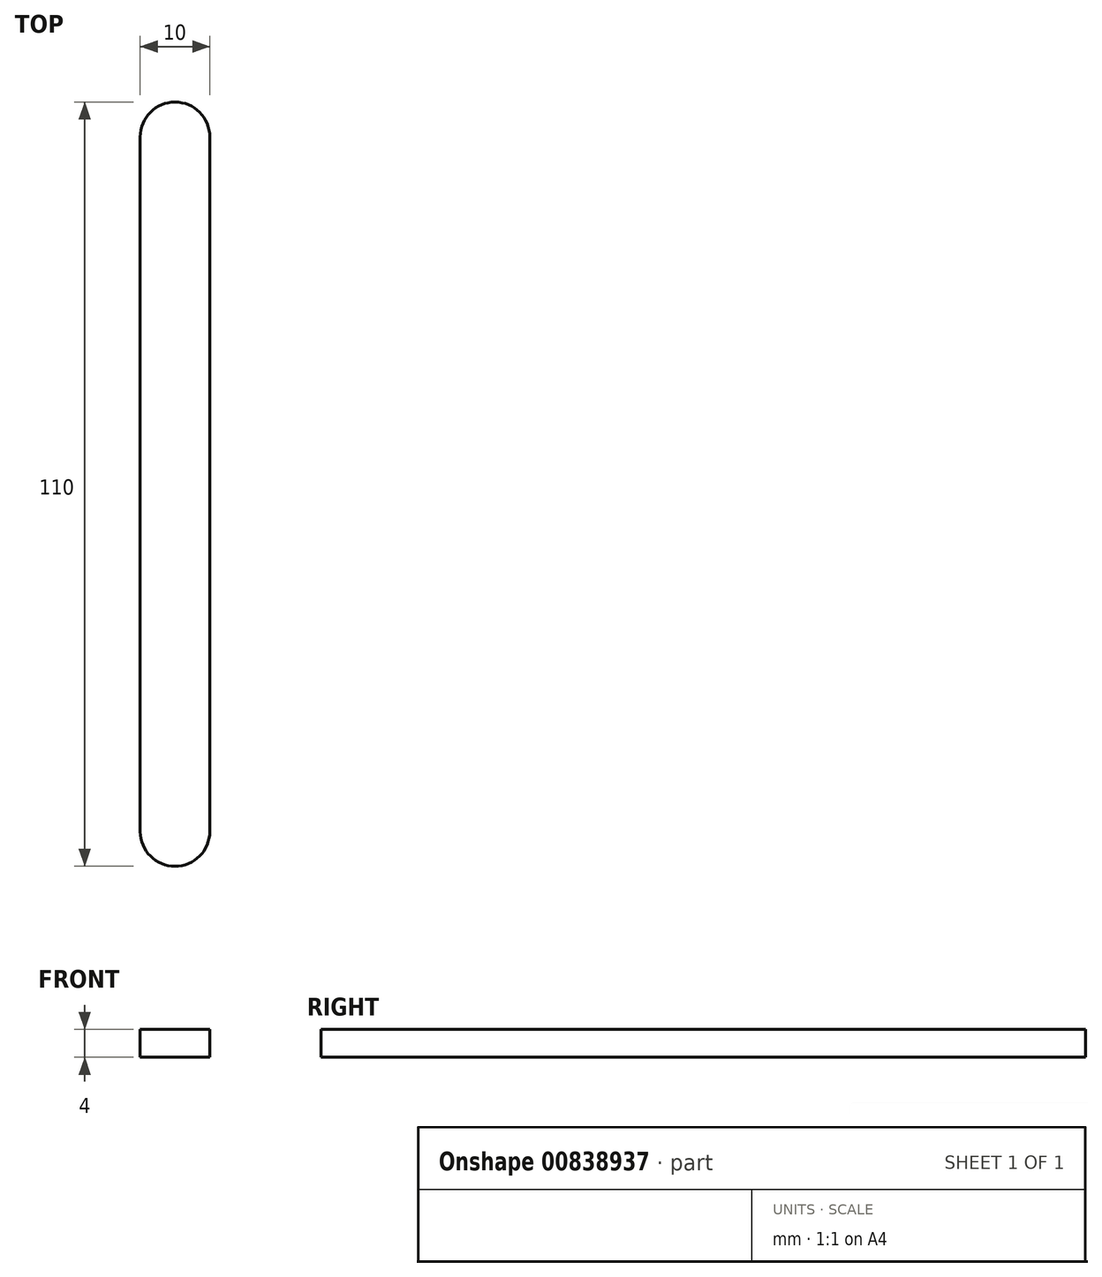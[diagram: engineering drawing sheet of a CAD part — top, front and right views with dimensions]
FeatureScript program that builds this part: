
annotation { "Feature Type Name" : "Feature", "Feature Type Description" : "" }
export const myFeature = defineFeature(function(context is Context, id is Id, definition is map)
    precondition{}
    {
        {
            var Q0;
            Q0=qCreatedBy(makeId("Top.planeOp"),FACE);
            var sketch = newSketch(context, id + "F0", { "sketchPlane" : qUnion([Q0])});
            skLineSegment(sketch, "E0", {"start": v(0, 0) * mm, "end": v(0, 47.66) * mm});
            skLineSegment(sketch, "E1", {"start": v(0, 47.66) * mm, "end": v(0, -52.34) * mm});
            skArc(sketch, "E2.0.startCap", {"start": v(-5, 47.66) * mm, "mid": v(0, 52.66) * mm, "end": v(5, 47.66) * mm});
            skArc(sketch, "E2.0.endCap", {"start": v(5, -52.34) * mm, "mid": v(0, -57.34) * mm, "end": v(-5, -52.34) * mm});
            skLineSegment(sketch, "E2.0.left", {"start": v(5, 47.66) * mm, "end": v(5, -52.34) * mm});
            skLineSegment(sketch, "E2.0.right", {"start": v(-5, 47.66) * mm, "end": v(-5, -52.34) * mm});
            skSolve(sketch);
        }
        {
            var Q0;
            Q0 = qSketchRegion(id + "F0", true);
            extrude(context, id + "F1", {"entities" : qUnion([Q0]), "depth" : 4 * mm, "offsetDistance" : 25 * mm});
        }
    });
